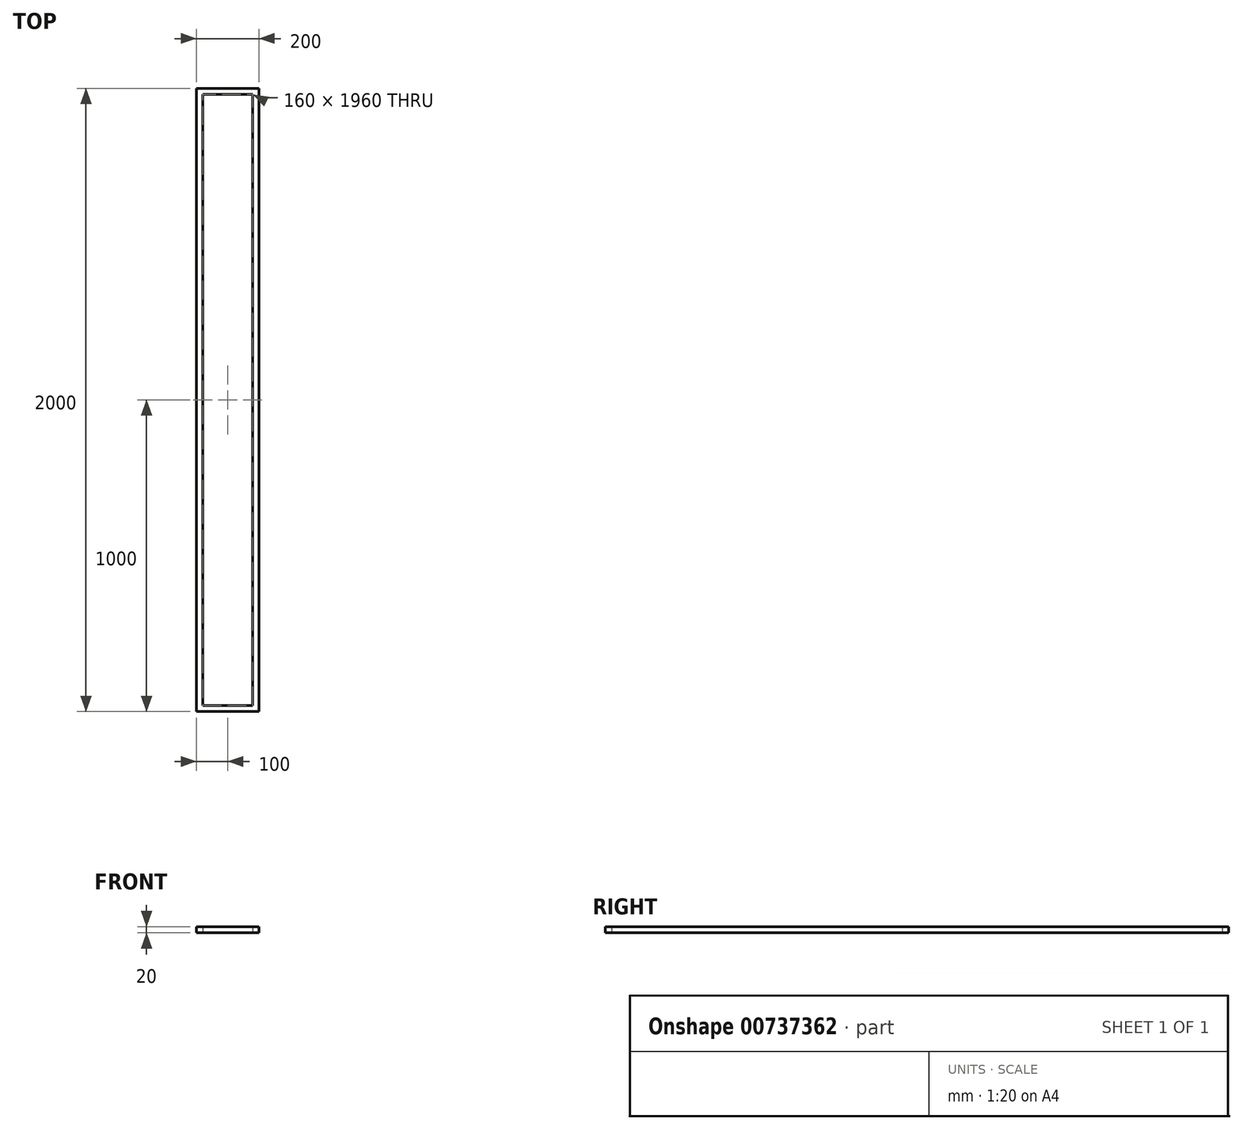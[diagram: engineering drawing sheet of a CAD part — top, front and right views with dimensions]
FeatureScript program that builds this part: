
annotation { "Feature Type Name" : "Feature", "Feature Type Description" : "" }
export const myFeature = defineFeature(function(context is Context, id is Id, definition is map)
    precondition{}
    {
        {
            var Q0;
            Q0=qCreatedBy(makeId("Top.planeOp"), FACE);
            var sketch = newSketch(context, id + "F0", { "sketchPlane" : qUnion([Q0])});
            skLineSegment(sketch, "E0.bottom", {"start": v(100, -1500) * mm, "end": v(-100, -1500) * mm});
            skLineSegment(sketch, "E0.top", {"start": v(100, 500) * mm, "end": v(-100, 500) * mm});
            skLineSegment(sketch, "E0.left", {"start": v(100, -1500) * mm, "end": v(100, 500) * mm});
            skLineSegment(sketch, "E0.right", {"start": v(-100, -1500) * mm, "end": v(-100, 500) * mm});
            skPoint(sketch, "E0.middle", {"position": v(0, -500) * mm});
            skLineSegment(sketch, "E1.bottom", {"start": v(80, -1480) * mm, "end": v(-80, -1480) * mm});
            skLineSegment(sketch, "E1.top", {"start": v(80, 480) * mm, "end": v(-80, 480) * mm});
            skLineSegment(sketch, "E1.left", {"start": v(80, -1480) * mm, "end": v(80, 480) * mm});
            skLineSegment(sketch, "E1.right", {"start": v(-80, -1480) * mm, "end": v(-80, 480) * mm});
            skSolve(sketch);
        }
        {
            var Q0;
            Q0=makeQuery(id+"F0.imprint","IMPRINT",FACE,{"disambiguationData":[TD([[makeQuery(id+"F0.imprint","IMPRINT",EDGE,{"derivedFrom":sQuery(id+"F0.wireOp",EDGE,"E0.bottom")}),-1.0]])]});
            extrude(context, id + "F1", {"entities" : qUnion([Q0]), "depth" : 20 * mm, "offsetDistance" : 25 * mm});
        }
    });
